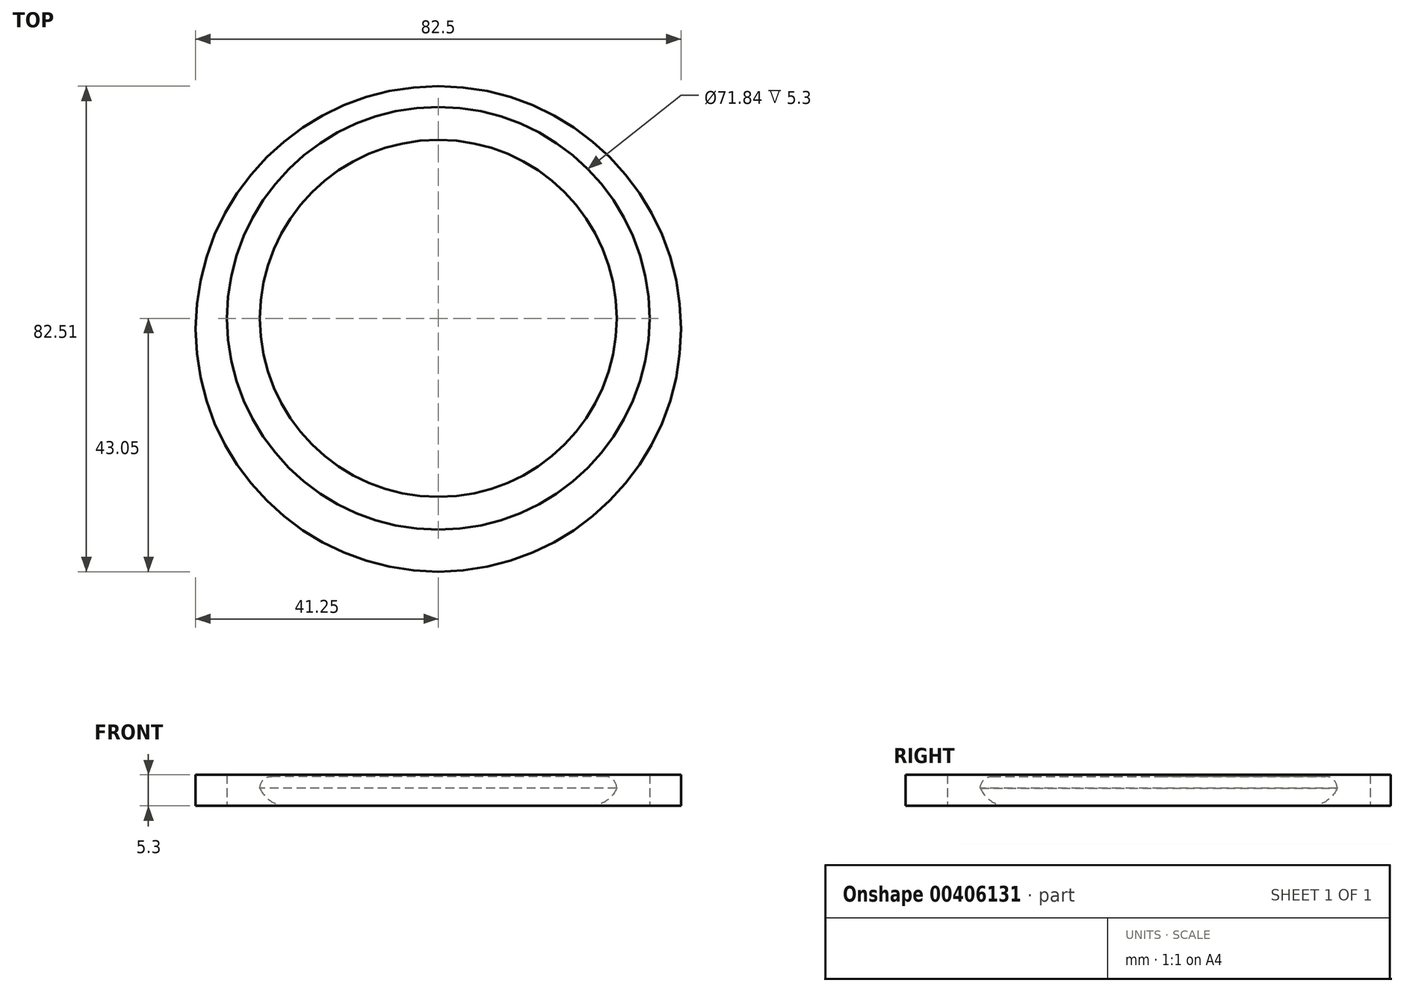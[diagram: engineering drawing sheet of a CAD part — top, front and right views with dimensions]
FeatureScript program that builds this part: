
annotation { "Feature Type Name" : "Feature", "Feature Type Description" : "" }
export const myFeature = defineFeature(function(context is Context, id is Id, definition is map)
    precondition{}
    {
        {
            var Q0;
            Q0=qCreatedBy(makeId("Top.planeOp"),FACE);
            var sketch = newSketch(context, id + "F0", { "sketchPlane" : qUnion([Q0])});
            skCircle(sketch, "E0", {"center": v(0, 0) * mm, "radius": 30.33 * mm});
            skSolve(sketch);
        }
        {
            var Q0;
            Q0 = qSketchRegion(id + "F0", true);
            extrude(context, id + "F1", {"entities" : qUnion([Q0]), "depth" : 5 * mm});
        }
        {
            var Q0;
            Q0=makeQuery(id+"F1.opExtrude","CAP_EDGE",EDGE,{"disambiguationData":[OSD([sQuery(id+"F0.wireOp",EDGE,"E0")])],"isStart":false});
            fillet(context, id + "F2", {"entities" : qUnion([Q0]), "radius" : 2 * mm, "tangentPropagation" : true, "allowEdgeOverflow" : false});
        }
        {
            var Q0;
            Q0=makeQuery(id+"F1.opExtrude","CAP_EDGE",EDGE,{"disambiguationData":[OSD([sQuery(id+"F0.wireOp",EDGE,"E0")])],"isStart":true});
            var Q1;
            {var subQ0=sQuery(id+"F0.wireOp",EDGE,"E0");Q1=makeQuery(id+"F2.opFillet","BLEND_EDGE",EDGE,{"blendedFrom":[makeQuery(id+"F1.opExtrude","CAP_EDGE",EDGE,{"disambiguationData":[OSD([subQ0])],"isStart":false}),makeQuery(id+"F1.opExtrude","CAP_FACE",FACE,{"disambiguationData":[OSD([subQ0])],"isStart":false})],"blendedInto":[makeQuery(id+"F1.opExtrude","CAP_FACE",FACE,{"disambiguationData":[OSD([subQ0])],"isStart":false})]});}
            var Q2;
            {var subQ0=sQuery(id+"F0.wireOp",EDGE,"E0");Q2=makeQuery(id+"F2.opFillet","BLEND_EDGE",EDGE,{"blendedFrom":[makeQuery(id+"F1.opExtrude","CAP_EDGE",EDGE,{"disambiguationData":[OSD([subQ0])],"isStart":false}),makeQuery(id+"F1.opExtrude","SWEPT_FACE",FACE,{"disambiguationData":[OSD([subQ0])]})],"blendedInto":[makeQuery(id+"F1.opExtrude","SWEPT_FACE",FACE,{"disambiguationData":[OSD([subQ0])]})]});}
            fillet(context, id + "F3", {"entities" : qUnion([Q0, Q1, Q2]), "radius" : 5 * mm, "tangentPropagation" : true, "allowEdgeOverflow" : false});
        }
        {
            var Q0;
            Q0=qCreatedBy(makeId("Top.planeOp"),FACE);
            var sketch = newSketch(context, id + "F4", { "sketchPlane" : qUnion([Q0])});
            skCircle(sketch, "E1", {"center": v(0, 0) * mm, "radius": 35.92 * mm});
            skCircle(sketch, "E2", {"center": v(0, -1.8) * mm, "radius": 41.25 * mm});
            skSolve(sketch);
        }
        {
            var Q0;
            Q0 = qSketchRegion(id + "F4", true);
            extrude(context, id + "F5", {"entities" : qUnion([Q0]), "operationType" : NewBodyOperationType.ADD, "depth" : 5.3 * mm});
        }
    });
